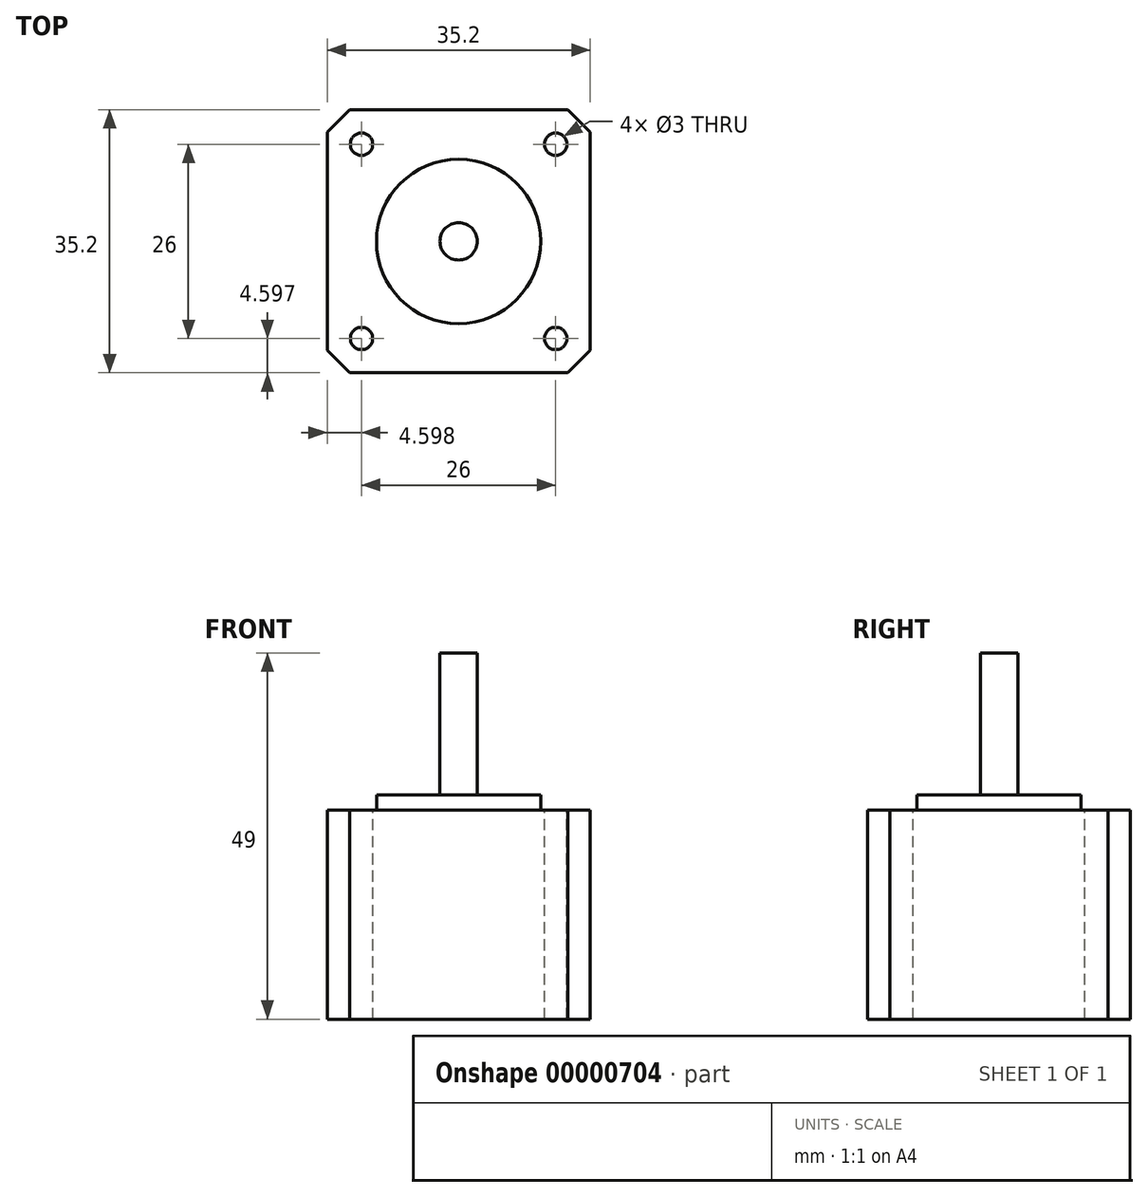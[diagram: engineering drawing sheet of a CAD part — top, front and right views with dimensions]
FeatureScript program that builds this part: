
annotation { "Feature Type Name" : "Feature", "Feature Type Description" : "" }
export const myFeature = defineFeature(function(context is Context, id is Id, definition is map)
    precondition{}
    {
        {
            var Q0;
            Q0=qCreatedBy(makeId("Top.planeOp"),FACE);
            cPlane(context, id + "F0", {"entities" : qUnion([Q0]), "cplaneType" : CPlaneType.OFFSET, "offset" : 150 * mm, "width" : 150 * mm, "height" : 150 * mm});
        }
        {
            var Q0;
            Q0=qCreatedBy(makeId("Top.planeOp"),FACE);
            var sketch = newSketch(context, id + "F1", { "sketchPlane" : qUnion([Q0])});
            skLineSegment(sketch, "E0.bottom", {"start": v(-37.07, 1.86) * mm, "end": v(-1.87, 1.86) * mm});
            skLineSegment(sketch, "E0.top", {"start": v(-37.07, -33.34) * mm, "end": v(-1.87, -33.34) * mm});
            skLineSegment(sketch, "E0.left", {"start": v(-37.07, 1.86) * mm, "end": v(-37.07, -33.34) * mm});
            skLineSegment(sketch, "E0.right", {"start": v(-1.87, 1.86) * mm, "end": v(-1.87, -33.34) * mm});
            skLineSegment(sketch, "E1", {"start": v(-37.07, 1.86) * mm, "end": v(-1.87, -33.34) * mm, "construction": true});
            skLineSegment(sketch, "E2", {"start": v(-1.87, 1.86) * mm, "end": v(-37.07, -33.34) * mm, "construction": true});
            skSolve(sketch);
        }
        {
            var Q0;
            Q0=makeQuery(id+"F1.imprint","IMPRINT",FACE,{"disambiguationData":[TD([[makeQuery(id+"F1.imprint","IMPRINT",EDGE,{"derivedFrom":sQuery(id+"F1.wireOp",EDGE,"E0.bottom")}),-1.0]])]});
            extrude(context, id + "F2", {"entities" : qUnion([Q0]), "depth" : 28 * mm});
        }
        {
            var Q0;
            Q0=makeQuery(id+"F2.opExtrude","SWEPT_EDGE",EDGE,{"disambiguationData":[OSD([sQuery(id+"F1.wireOp",EDGE,"E0.top"),sQuery(id+"F1.wireOp",EDGE,"E0.right")])]});
            var Q1;
            Q1=makeQuery(id+"F2.opExtrude","SWEPT_EDGE",EDGE,{"disambiguationData":[OSD([sQuery(id+"F1.wireOp",EDGE,"E0.bottom"),sQuery(id+"F1.wireOp",EDGE,"E0.right")])]});
            var Q2;
            Q2=makeQuery(id+"F2.opExtrude","SWEPT_EDGE",EDGE,{"disambiguationData":[OSD([sQuery(id+"F1.wireOp",EDGE,"E0.bottom"),sQuery(id+"F1.wireOp",EDGE,"E0.left")])]});
            var Q3;
            Q3=makeQuery(id+"F2.opExtrude","SWEPT_EDGE",EDGE,{"disambiguationData":[OSD([sQuery(id+"F1.wireOp",EDGE,"E0.top"),sQuery(id+"F1.wireOp",EDGE,"E0.left")])]});
            chamfer(context, id + "F3", {"entities" : qUnion([Q0, Q1, Q2, Q3]), "width" : 3 * mm, "tangentPropagation" : true});
        }
        {
            var Q0;
            Q0=makeQuery(id+"F2.opExtrude","CAP_FACE",FACE,{"disambiguationData":[OSD([sQuery(id+"F1.wireOp",EDGE,"E0.bottom"),sQuery(id+"F1.wireOp",EDGE,"E0.top"),sQuery(id+"F1.wireOp",EDGE,"E0.left"),sQuery(id+"F1.wireOp",EDGE,"E0.right")])],"isStart":false});
            var sketch = newSketch(context, id + "F4", { "sketchPlane" : qUnion([Q0])});
            skLineSegment(sketch, "E3", {"start": v(-35.57, 0.36) * mm, "end": v(-3.37, -31.84) * mm, "construction": true});
            skLineSegment(sketch, "E4", {"start": v(-35.57, -31.84) * mm, "end": v(-3.37, 0.36) * mm, "construction": true});
            skCircle(sketch, "E5", {"center": v(-32.47, -2.74) * mm, "radius": 1.5 * mm});
            skCircle(sketch, "E6", {"center": v(-6.47, -2.74) * mm, "radius": 1.5 * mm});
            skCircle(sketch, "E7", {"center": v(-6.47, -28.74) * mm, "radius": 1.5 * mm});
            skCircle(sketch, "E8", {"center": v(-32.47, -28.74) * mm, "radius": 1.5 * mm});
            skSolve(sketch);
        }
        {
            var Q0;
            {Q0=qUnion([makeQuery(id+"F4.imprint","IMPRINT",FACE,{"disambiguationData":[TD([[makeQuery(id+"F4.imprint","IMPRINT",EDGE,{"derivedFrom":sQuery(id+"F4.wireOp",EDGE,"E5")}),1.0]])]}),makeQuery(id+"F4.imprint","IMPRINT",FACE,{"disambiguationData":[TD([[makeQuery(id+"F4.imprint","IMPRINT",EDGE,{"derivedFrom":sQuery(id+"F4.wireOp",EDGE,"E6")}),1.0]])]}),makeQuery(id+"F4.imprint","IMPRINT",FACE,{"disambiguationData":[TD([[makeQuery(id+"F4.imprint","IMPRINT",EDGE,{"derivedFrom":sQuery(id+"F4.wireOp",EDGE,"E7")}),1.0]])]}),makeQuery(id+"F4.imprint","IMPRINT",FACE,{"disambiguationData":[TD([[makeQuery(id+"F4.imprint","IMPRINT",EDGE,{"derivedFrom":sQuery(id+"F4.wireOp",EDGE,"E8")}),1.0]])]})]);}
            extrude(context, id + "F5", {"entities" : qUnion([Q0]), "operationType" : NewBodyOperationType.REMOVE, "endBound" : BoundingType.THROUGH_ALL, "oppositeDirection" : true, "depth" : 2 * mm});
        }
        {
            var Q0;
            Q0=makeQuery(id+"F2.opExtrude","CAP_FACE",FACE,{"disambiguationData":[OSD([sQuery(id+"F1.wireOp",EDGE,"E0.bottom"),sQuery(id+"F1.wireOp",EDGE,"E0.top"),sQuery(id+"F1.wireOp",EDGE,"E0.left"),sQuery(id+"F1.wireOp",EDGE,"E0.right")])],"isStart":false});
            var sketch = newSketch(context, id + "F6", { "sketchPlane" : qUnion([Q0])});
            skLineSegment(sketch, "E9", {"start": v(-34.07, 1.86) * mm, "end": v(-4.87, -33.34) * mm, "construction": true});
            skLineSegment(sketch, "E10", {"start": v(-1.87, -1.14) * mm, "end": v(-37.07, -30.34) * mm, "construction": true});
            skCircle(sketch, "E11", {"center": v(-19.47, -15.74) * mm, "radius": 11 * mm});
            skSolve(sketch);
        }
        {
            var Q0;
            Q0=makeQuery(id+"F6.imprint","IMPRINT",FACE,{"disambiguationData":[TD([[makeQuery(id+"F6.imprint","IMPRINT",EDGE,{"derivedFrom":sQuery(id+"F6.wireOp",EDGE,"E11")}),1.0]])]});
            extrude(context, id + "F7", {"entities" : qUnion([Q0]), "operationType" : NewBodyOperationType.ADD, "depth" : 2 * mm});
        }
        {
            var Q0;
            Q0=makeQuery(id+"F7.opExtrude","CAP_FACE",FACE,{"disambiguationData":[OSD([sQuery(id+"F6.wireOp",EDGE,"E11")])],"isStart":false});
            var sketch = newSketch(context, id + "F8", { "sketchPlane" : qUnion([Q0])});
            skCircle(sketch, "E12", {"center": v(-19.47, -15.74) * mm, "radius": 2.5 * mm});
            skSolve(sketch);
        }
        {
            var Q0;
            Q0=makeQuery(id+"F8.imprint","IMPRINT",FACE,{"disambiguationData":[TD([[makeQuery(id+"F8.imprint","IMPRINT",EDGE,{"derivedFrom":sQuery(id+"F8.wireOp",EDGE,"E12")}),1.0]])]});
            extrude(context, id + "F9", {"entities" : qUnion([Q0]), "operationType" : NewBodyOperationType.ADD, "depth" : 19 * mm});
        }
        {
            var Q0;
            Q0=qCreatedBy(id+"F0.planeOp",FACE);
            var sketch = newSketch(context, id + "F10", { "sketchPlane" : qUnion([Q0])});
            skCircle(sketch, "E13", {"center": v(-32.47, -2.74) * mm, "radius": 1.5 * mm});
            skCircle(sketch, "E14", {"center": v(-6.47, -2.74) * mm, "radius": 1.5 * mm});
            skCircle(sketch, "E15", {"center": v(-6.47, -28.74) * mm, "radius": 1.5 * mm});
            skCircle(sketch, "E16", {"center": v(-32.47, -28.74) * mm, "radius": 1.5 * mm});
            skLineSegment(sketch, "E17", {"start": v(-37.07, -1.14) * mm, "end": v(-34.07, 1.86) * mm});
            skLineSegment(sketch, "E18", {"start": v(-34.07, 1.86) * mm, "end": v(-4.87, 1.86) * mm});
            skLineSegment(sketch, "E19", {"start": v(-4.87, 1.86) * mm, "end": v(-1.87, -1.14) * mm});
            skLineSegment(sketch, "E20", {"start": v(-1.87, -1.14) * mm, "end": v(-1.87, -25.74) * mm});
            skLineSegment(sketch, "E21", {"start": v(-4.87, -33.34) * mm, "end": v(-34.07, -33.34) * mm});
            skLineSegment(sketch, "E22", {"start": v(-37.07, -25.74) * mm, "end": v(-37.07, -1.14) * mm});
            skLineSegment(sketch, "E23", {"start": v(-32.47, -2.74) * mm, "end": v(-6.47, -28.74) * mm, "construction": true});
            skLineSegment(sketch, "E24", {"start": v(-6.47, -2.74) * mm, "end": v(-32.47, -28.74) * mm, "construction": true});
            skCircle(sketch, "E25", {"center": v(-19.47, -15.74) * mm, "radius": 11.5 * mm});
            skLineSegment(sketch, "E26", {"start": v(-34.07, -33.34) * mm, "end": v(-54.74, -33.34) * mm});
            skLineSegment(sketch, "E27", {"start": v(-55.45, -33.05) * mm, "end": v(-57.86, -30.64) * mm});
            skLineSegment(sketch, "E28", {"start": v(-58.16, -29.93) * mm, "end": v(-58.16, -29.16) * mm});
            skLineSegment(sketch, "E29", {"start": v(-57.86, -28.45) * mm, "end": v(-55.45, -26.04) * mm});
            skLineSegment(sketch, "E30", {"start": v(-54.74, -25.74) * mm, "end": v(-37.07, -25.74) * mm});
            skPoint(sketch, "E31.visualSharp", {"position": v(-55.16, -25.74) * mm});
            skArc(sketch, "E31.filletArc", {"start": v(-54.74, -25.74) * mm, "mid": v(-55.12, -25.82) * mm, "end": v(-55.45, -26.04) * mm});
            skPoint(sketch, "E32.visualSharp", {"position": v(-55.16, -33.34) * mm});
            skArc(sketch, "E32.filletArc", {"start": v(-55.45, -33.05) * mm, "mid": v(-55.12, -33.27) * mm, "end": v(-54.74, -33.34) * mm});
            skPoint(sketch, "E33.visualSharp", {"position": v(-58.16, -30.34) * mm});
            skArc(sketch, "E33.filletArc", {"start": v(-58.16, -29.93) * mm, "mid": v(-58.08, -30.31) * mm, "end": v(-57.86, -30.64) * mm});
            skPoint(sketch, "E34.visualSharp", {"position": v(-58.16, -28.74) * mm});
            skArc(sketch, "E34.filletArc", {"start": v(-57.86, -28.45) * mm, "mid": v(-58.08, -28.77) * mm, "end": v(-58.16, -29.16) * mm});
            skLineSegment(sketch, "E35", {"start": v(-19.47, -15.74) * mm, "end": v(-19.47, -24.65) * mm, "construction": true});
            skArc(sketch, "E36.0.MirrorCS", {"start": v(19.21, -29.93) * mm, "mid": v(19.14, -30.31) * mm, "end": v(18.92, -30.64) * mm});
            skArc(sketch, "E36.1.MirrorCS", {"start": v(16.5, -33.05) * mm, "mid": v(16.18, -33.27) * mm, "end": v(15.8, -33.34) * mm});
            skLineSegment(sketch, "E36.2.MirrorCS", {"start": v(19.21, -29.93) * mm, "end": v(19.21, -29.16) * mm});
            skPoint(sketch, "E36.3.MirrorP", {"position": v(19.21, -30.34) * mm});
            skArc(sketch, "E36.4.MirrorCS", {"start": v(18.92, -28.45) * mm, "mid": v(19.14, -28.77) * mm, "end": v(19.21, -29.16) * mm});
            skArc(sketch, "E36.5.MirrorCS", {"start": v(15.8, -25.74) * mm, "mid": v(16.18, -25.82) * mm, "end": v(16.5, -26.04) * mm});
            skLineSegment(sketch, "E36.6.MirrorCS", {"start": v(15.8, -25.74) * mm, "end": v(-1.87, -25.74) * mm});
            skPoint(sketch, "E36.7.MirrorP", {"position": v(16.21, -33.34) * mm});
            skPoint(sketch, "E36.8.MirrorP", {"position": v(19.21, -28.74) * mm});
            skLineSegment(sketch, "E36.9.MirrorCS", {"start": v(-4.87, -33.34) * mm, "end": v(15.8, -33.34) * mm});
            skPoint(sketch, "E36.10.MirrorP", {"position": v(16.21, -25.74) * mm});
            skLineSegment(sketch, "E36.11.MirrorCS", {"start": v(16.5, -33.05) * mm, "end": v(18.92, -30.64) * mm});
            skLineSegment(sketch, "E36.12.MirrorCS", {"start": v(18.92, -28.45) * mm, "end": v(16.5, -26.04) * mm});
            skPoint(sketch, "E37.end.orphan", {"position": v(-37.07, -30.34) * mm});
            skLineSegment(sketch, "E38", {"start": v(-58.16, -29.54) * mm, "end": v(-36.41, -29.54) * mm, "construction": true});
            skCircle(sketch, "E39", {"center": v(-54.74, -29.54) * mm, "radius": 1.5 * mm});
            skCircle(sketch, "E40", {"center": v(-47.97, -29.54) * mm, "radius": 1.5 * mm});
            skCircle(sketch, "E41.0.MirrorC", {"center": v(9.02, -29.54) * mm, "radius": 1.5 * mm});
            skCircle(sketch, "E42.0.MirrorC", {"center": v(15.8, -29.54) * mm, "radius": 1.5 * mm});
            skSolve(sketch);
        }
        {
            var Q0;
            Q0=makeQuery(id+"F10.imprint","IMPRINT",FACE,{"disambiguationData":[TD([[makeQuery(id+"F10.imprint","IMPRINT",EDGE,{"derivedFrom":sQuery(id+"F10.wireOp",EDGE,"E13")}),-1.0]])]});
            extrude(context, id + "F11", {"entities" : qUnion([Q0]), "operationType" : NewBodyOperationType.ADD, "depth" : 3 * mm});
        }
        {
            var Q0;
            Q0=makeQuery(id+"F11.opExtrude","SWEPT_BODY",BODY,{"disambiguationData":[OSD([sQuery(id+"F10.wireOp",EDGE,"E13"),sQuery(id+"F10.wireOp",EDGE,"E14"),sQuery(id+"F10.wireOp",EDGE,"E15"),sQuery(id+"F10.wireOp",EDGE,"E16"),sQuery(id+"F10.wireOp",EDGE,"E17"),sQuery(id+"F10.wireOp",EDGE,"E18"),sQuery(id+"F10.wireOp",EDGE,"E19"),sQuery(id+"F10.wireOp",EDGE,"E20"),sQuery(id+"F10.wireOp",EDGE,"E22"),sQuery(id+"F10.wireOp",EDGE,"E25"),sQuery(id+"F10.wireOp",EDGE,"E26"),sQuery(id+"F10.wireOp",EDGE,"E27"),sQuery(id+"F10.wireOp",EDGE,"E28"),sQuery(id+"F10.wireOp",EDGE,"E29"),sQuery(id+"F10.wireOp",EDGE,"E30"),sQuery(id+"F10.wireOp",EDGE,"E31.filletArc"),sQuery(id+"F10.wireOp",EDGE,"E32.filletArc"),sQuery(id+"F10.wireOp",EDGE,"E33.filletArc"),sQuery(id+"F10.wireOp",EDGE,"E34.filletArc"),sQuery(id+"F10.wireOp",EDGE,"E36.0.MirrorCS"),sQuery(id+"F10.wireOp",EDGE,"E36.1.MirrorCS"),sQuery(id+"F10.wireOp",EDGE,"E36.2.MirrorCS"),sQuery(id+"F10.wireOp",EDGE,"E36.4.MirrorCS"),sQuery(id+"F10.wireOp",EDGE,"E36.5.MirrorCS"),sQuery(id+"F10.wireOp",EDGE,"E36.6.MirrorCS"),sQuery(id+"F10.wireOp",EDGE,"E36.11.MirrorCS"),sQuery(id+"F10.wireOp",EDGE,"E36.12.MirrorCS"),sQuery(id+"F10.wireOp",EDGE,"E39"),sQuery(id+"F10.wireOp",EDGE,"E40"),sQuery(id+"F10.wireOp",EDGE,"E41.0.MirrorC"),sQuery(id+"F10.wireOp",EDGE,"E42.0.MirrorC")])]});
            deleteBodies(context, id + "F12", {"entities" : qUnion([Q0])});
        }
    });
